# Revit family: Toilet_Seat-American_Standard-Aquawash-8033A65G.020
name_source: partatom
category: Specialty Equipment
units: mm (PartAtom-declared; Revit-internal decimal feet)

## family parameters
Always vertical = No
Cut with Voids When Loaded = No
OmniClass Number = 23.45.05.21.14.11
OmniClass Title = Water Closet Seats
Part Type = Normal
Room Calculation Point = No
Round Connector Dimension = Use Diameter
Shared = Yes
Work Plane-Based = Yes

## types (1)
- 8033A65G.020
    760-01-0009.0070A T-Valve for Water Supply Hose = No
    760-01-0010.0070A Water Supply Hose = No
    760-02-0027.0070A Seat Handle = No
    760-02-0045.0070A Nozzle Tip Set (2 Nozzles) = No
    760-06-0046.0070A Seat Mounting Kit = No
    Assembly Code = C1030200
    Bowl Width = 8 5/16"
    Default Elevation = 0"
    Description = AquaWash® Slim Non-Electric SpaLet® Bidet Seat With Manual Operation
    Finish = Plastic-American Standard-020-White
    Height = 2 3/16"
    Hole Location = 5 1/2"
    IAPMO Compliance = ASME A112.4.2/CSA B45.16
    Installation Instruction Link = https://lixil.cdn.celum.cloud
    Installation Type = Surface Mounted
    Length = 19 5/16"
    Manufacturer = American Standard
    Material = Plastic-American Standard-020-White
    Model = 8033A65G.020
    Price = Prices may vary. Please consult Manufacturer Representative for most up-to-date price list.
    Product Documentation Link = https://lixil.cdn.celum.cloud
    Product Page URL = https://www.americanstandard-us.com
    URL = https://www.americanstandard-us.com
    Warranty Information = 1 Year Limited Warranty
    Width = 14 9/16"

## geometry (parser evidence)
native form markers: Sweep x2
no freeform markers — native parametric forms only
